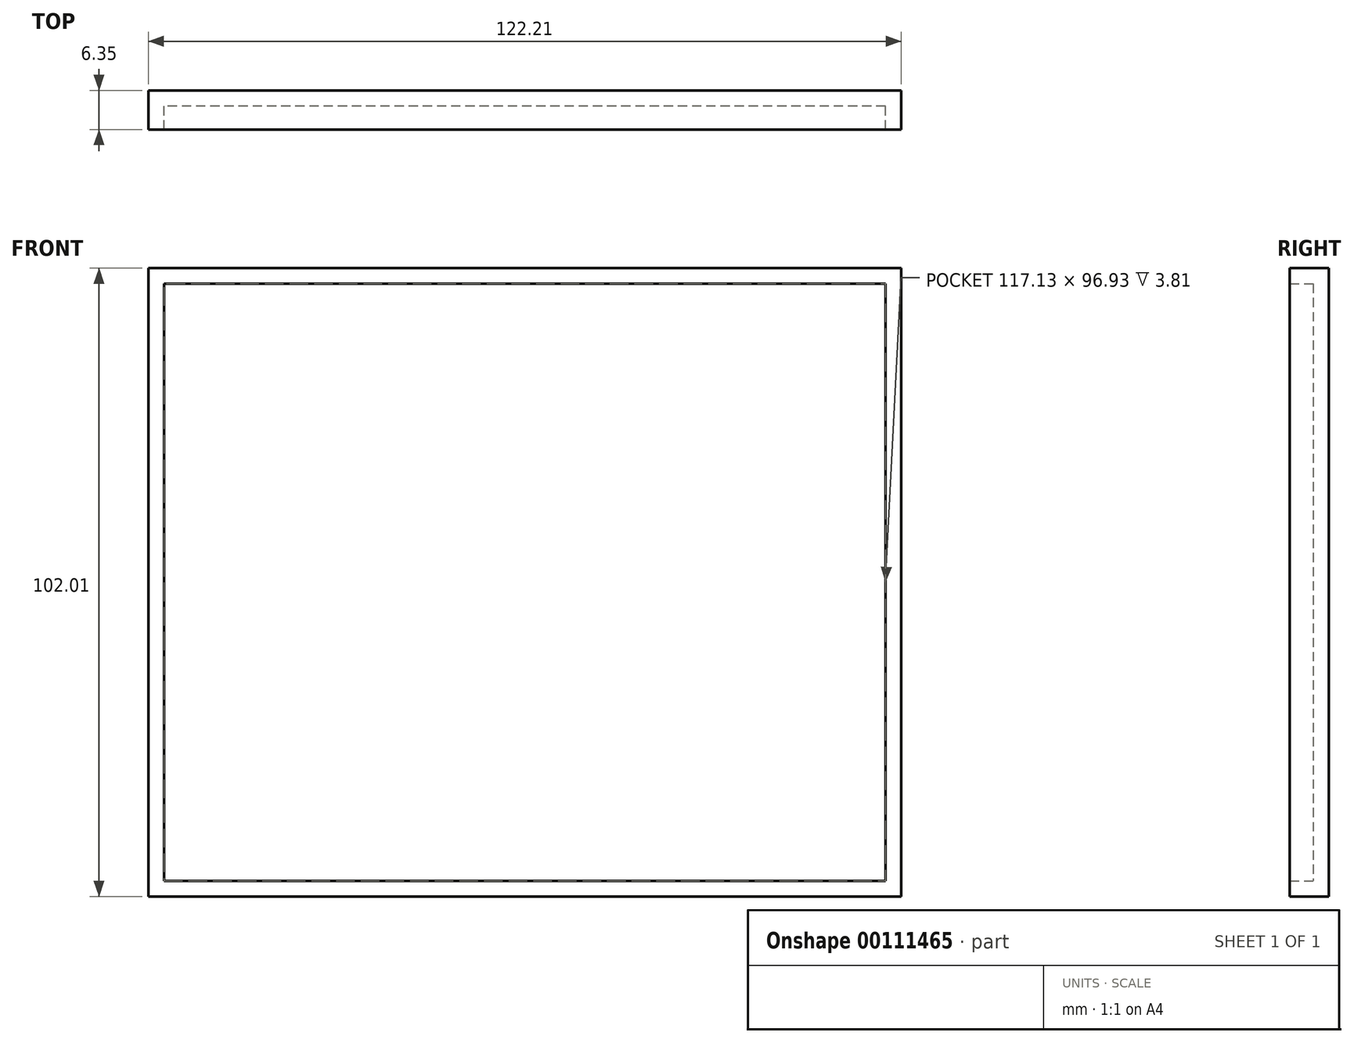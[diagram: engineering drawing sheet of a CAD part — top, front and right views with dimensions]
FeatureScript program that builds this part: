
annotation { "Feature Type Name" : "Feature", "Feature Type Description" : "" }
export const myFeature = defineFeature(function(context is Context, id is Id, definition is map)
    precondition{}
    {
        {
            var Q0;
            Q0=qCreatedBy(makeId("Front.planeOp"),FACE);
            var sketch = newSketch(context, id + "F0", { "sketchPlane" : qUnion([Q0])});
            skFitSpline(sketch, "E0", {"points": [v(21.18, -36.7) * mm, v(31.85, 0) * mm, v(41.07, 8.38) * mm], "startDerivative": vector(32.84, 105.07) * mm, "endDerivative": vector(48.45, -1.9) * mm});
            skLineSegment(sketch, "E1", {"start": v(-9.59, -29.8) * mm, "end": v(-3.38, -15.75) * mm});
            skLineSegment(sketch, "E2", {"start": v(-3.38, -15.75) * mm, "end": v(-2.04, -30.36) * mm});
            skLineSegment(sketch, "E3", {"start": v(-20.24, 43.31) * mm, "end": v(-26.58, 16.57) * mm});
            skLineSegment(sketch, "E4", {"start": v(-13.76, 43.7) * mm, "end": v(-20.2, 16.3) * mm});
            skLineSegment(sketch, "E5", {"start": v(13.48, 44.98) * mm, "end": v(6.7, 18.33) * mm});
            skLineSegment(sketch, "E6", {"start": v(19.68, 43.84) * mm, "end": v(11.83, 16.3) * mm});
            skFitSpline(sketch, "E7", {"points": [v(11.83, 16.3) * mm, v(12.92, 12.66) * mm, v(5.02, -0.39) * mm], "startDerivative": vector(12.5, -5.36) * mm, "endDerivative": vector(-21.83, -25.53) * mm});
            skFitSpline(sketch, "E8", {"points": [v(-20.2, 16.3) * mm, v(-18, 9.61) * mm, v(-26.06, -5.16) * mm], "startDerivative": vector(16.66, -3.61) * mm, "endDerivative": vector(-20.72, -31.47) * mm});
            skFitSpline(sketch, "E9", {"points": [v(-26.58, 16.57) * mm, v(-29.2, 14.6) * mm, v(-26.06, -5.17) * mm], "startDerivative": vector(-16.03, -5.86) * mm, "endDerivative": vector(6.14, -32.1) * mm});
            skArc(sketch, "E10", {"start": v(-20.24, 43.31) * mm, "mid": v(-34.71, 37.22) * mm, "end": v(-46.45, 26.8) * mm});
            skArc(sketch, "E11", {"start": v(13.48, 44.98) * mm, "mid": v(-0.24, 46.38) * mm, "end": v(-13.76, 43.7) * mm});
            skArc(sketch, "E12", {"start": v(48.05, 32.08) * mm, "mid": v(34.69, 39.94) * mm, "end": v(19.68, 43.84) * mm});
            skArc(sketch, "E13", {"start": v(-9.59, -29.8) * mm, "mid": v(-31.12, -30.87) * mm, "end": v(-49.99, -41.3) * mm});
            skArc(sketch, "E14", {"start": v(21.26, -36.44) * mm, "mid": v(10.07, -31.62) * mm, "end": v(-2.04, -30.36) * mm});
            skLineSegment(sketch, "E15", {"start": v(48.05, 32.08) * mm, "end": v(41.07, 8.38) * mm});
            skLineSegment(sketch, "E16", {"start": v(-46.45, 26.8) * mm, "end": v(-49.96, 0.9) * mm});
            skFitSpline(sketch, "E17", {"points": [v(-49.96, 0.9) * mm, v(-43.79, -5.48) * mm, v(-49.99, -41.3) * mm], "startDerivative": vector(32.82, -8.11) * mm, "endDerivative": vector(-23.38, -98.89) * mm});
            skFitSpline(sketch, "E18", {"points": [v(6.7, 18.33) * mm, v(2.02, 13.07) * mm, v(5.02, -0.39) * mm], "startDerivative": vector(-35.5, -4.34) * mm, "endDerivative": vector(8.56, -40.04) * mm});
            skSolve(sketch);
        }
        {
            var Q0;
            Q0=sQuery(id+"F0.wireOp",EDGE,"E10");
            var Q1;
            Q1=sQuery(id+"F0.wireOp",EDGE,"E16");
            var Q2;
            Q2=sQuery(id+"F0.wireOp",EDGE,"E17");
            var Q3;
            Q3=sQuery(id+"F0.wireOp",EDGE,"E13");
            var Q4;
            Q4=sQuery(id+"F0.wireOp",EDGE,"E1");
            var Q5;
            Q5=sQuery(id+"F0.wireOp",EDGE,"E2");
            var Q6;
            Q6=sQuery(id+"F0.wireOp",EDGE,"E14");
            var Q7;
            Q7=sQuery(id+"F0.wireOp",EDGE,"E0");
            var Q8;
            Q8=sQuery(id+"F0.wireOp",EDGE,"E15");
            var Q9;
            Q9=sQuery(id+"F0.wireOp",EDGE,"E12");
            var Q10;
            Q10=sQuery(id+"F0.wireOp",EDGE,"E6");
            var Q11;
            Q11=sQuery(id+"F0.wireOp",EDGE,"E7");
            var Q12;
            Q12=sQuery(id+"F0.wireOp",EDGE,"E18");
            var Q13;
            Q13=sQuery(id+"F0.wireOp",EDGE,"E5");
            var Q14;
            Q14=sQuery(id+"F0.wireOp",EDGE,"E11");
            var Q15;
            Q15=sQuery(id+"F0.wireOp",EDGE,"E4");
            var Q16;
            Q16=sQuery(id+"F0.wireOp",EDGE,"E3");
            var Q17;
            Q17=sQuery(id+"F0.wireOp",EDGE,"E9");
            var Q18;
            Q18=sQuery(id+"F0.wireOp",EDGE,"E8");
            extrude(context, id + "F1", {"bodyType" : ToolBodyType.SURFACE, "surfaceEntities" : qUnion([Q0, Q1, Q2, Q3, Q4, Q5, Q6, Q7, Q8, Q9, Q10, Q11, Q12, Q13, Q14, Q15, Q16, Q17, Q18]), "depth" : 12.7 * mm});
        }
        {
            var Q0;
            Q0=qCreatedBy(makeId("Front.planeOp"),FACE);
            var sketch = newSketch(context, id + "F2", { "sketchPlane" : qUnion([Q0])});
            skLineSegment(sketch, "E19.bottom", {"start": v(58.5, 53.94) * mm, "end": v(-63.71, 53.94) * mm});
            skLineSegment(sketch, "E19.top", {"start": v(58.5, -48.07) * mm, "end": v(-63.71, -48.07) * mm});
            skLineSegment(sketch, "E19.left", {"start": v(58.5, 53.94) * mm, "end": v(58.5, -48.07) * mm});
            skLineSegment(sketch, "E19.right", {"start": v(-63.71, 53.94) * mm, "end": v(-63.71, -48.07) * mm});
            skSolve(sketch);
        }
        {
            var Q0;
            Q0 = qSketchRegion(id + "F2", true);
            extrude(context, id + "F3", {"entities" : qUnion([Q0]), "depth" : 6.35 * mm});
        }
        {
            var Q0;
            Q0=makeQuery(id+"F3.opExtrude","CAP_FACE",FACE,{"disambiguationData":[OSD([sQuery(id+"F2.wireOp",EDGE,"E19.bottom"),sQuery(id+"F2.wireOp",EDGE,"E19.top"),sQuery(id+"F2.wireOp",EDGE,"E19.left"),sQuery(id+"F2.wireOp",EDGE,"E19.right")])],"isStart":false});
            shell(context, id + "F4", {"entities" : qUnion([Q0]), "thickness" : 2.54 * mm});
        }
    });
